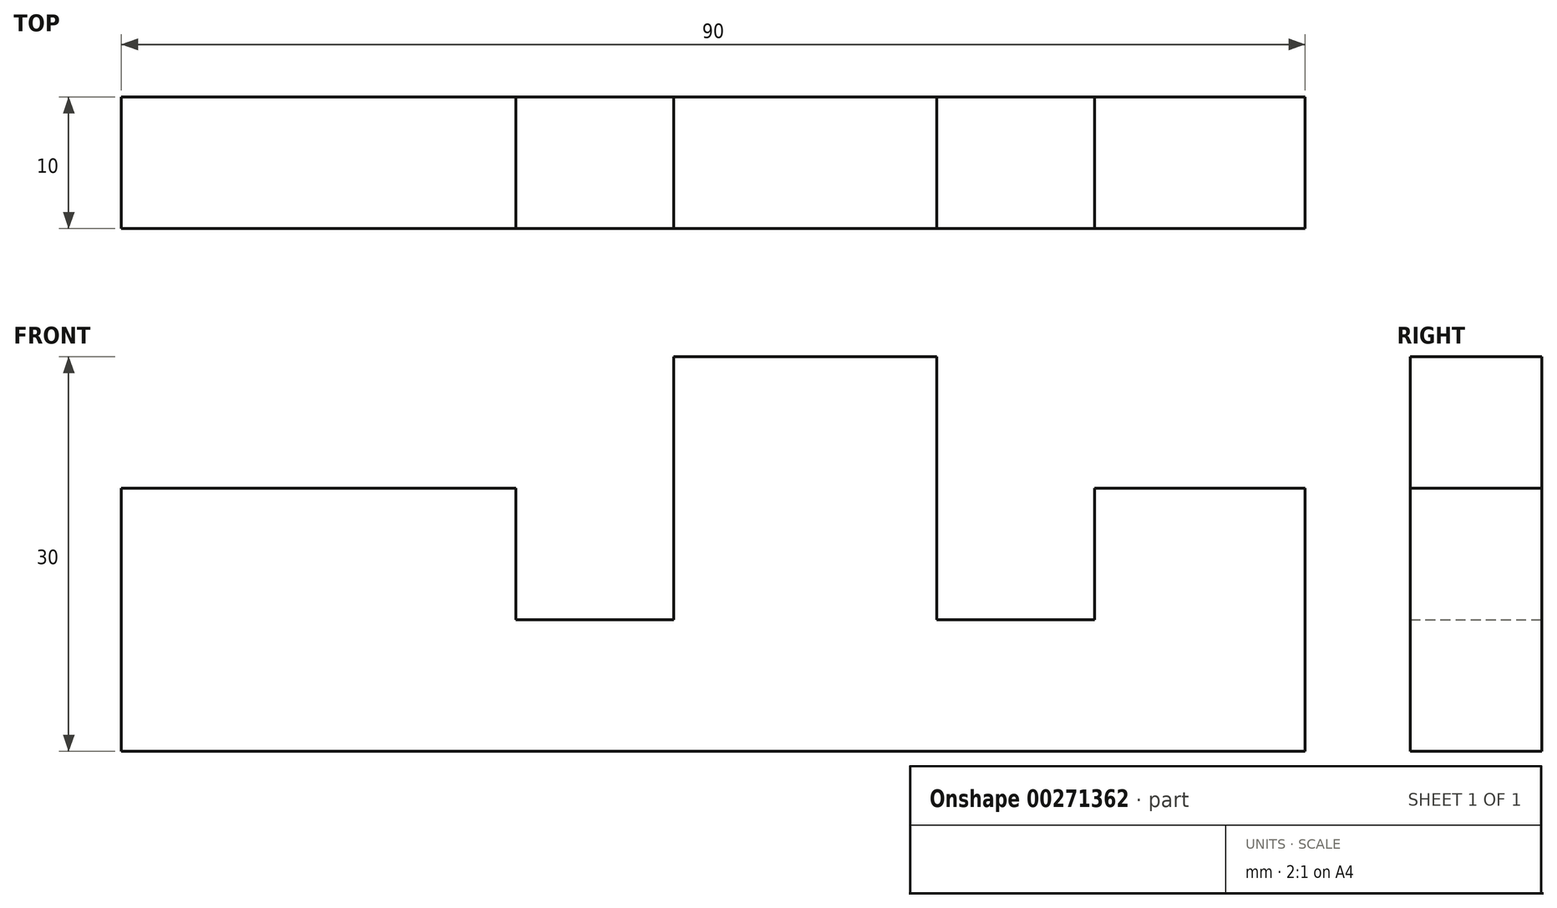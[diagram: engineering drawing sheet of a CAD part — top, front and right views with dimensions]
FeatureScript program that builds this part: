
annotation { "Feature Type Name" : "Feature", "Feature Type Description" : "" }
export const myFeature = defineFeature(function(context is Context, id is Id, definition is map)
    precondition{}
    {
        {
            var Q0;
            Q0=qCreatedBy(makeId("Front.planeOp"),FACE);
            var sketch = newSketch(context, id + "F0", { "sketchPlane" : qUnion([Q0])});
            skLineSegment(sketch, "E0", {"start": v(0, 0) * mm, "end": v(90, 0) * mm});
            skLineSegment(sketch, "E1", {"start": v(90, 0) * mm, "end": v(90, 20) * mm});
            skLineSegment(sketch, "E2", {"start": v(0, 20) * mm, "end": v(0, 0) * mm});
            skLineSegment(sketch, "E3", {"start": v(0, 20) * mm, "end": v(30, 20) * mm});
            skLineSegment(sketch, "E4", {"start": v(30, 20) * mm, "end": v(30, 10) * mm});
            skLineSegment(sketch, "E5", {"start": v(30, 10) * mm, "end": v(42, 10) * mm});
            skLineSegment(sketch, "E6", {"start": v(42, 10) * mm, "end": v(42, 30) * mm});
            skLineSegment(sketch, "E7", {"start": v(42, 30) * mm, "end": v(62, 30) * mm});
            skLineSegment(sketch, "E8", {"start": v(62, 30) * mm, "end": v(62, 10) * mm});
            skLineSegment(sketch, "E9", {"start": v(62, 10) * mm, "end": v(74, 10) * mm});
            skLineSegment(sketch, "E10", {"start": v(74, 10) * mm, "end": v(74, 20) * mm});
            skLineSegment(sketch, "E11", {"start": v(74, 20) * mm, "end": v(90, 20) * mm});
            skSolve(sketch);
        }
        {
            var Q0;
            Q0 = qSketchRegion(id + "F0", true);
            extrude(context, id + "F1", {"entities" : qUnion([Q0]), "depth" : 10 * mm});
        }
    });
